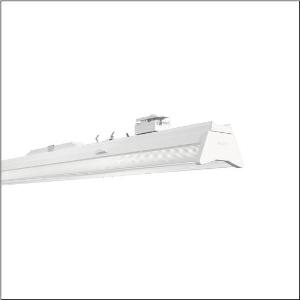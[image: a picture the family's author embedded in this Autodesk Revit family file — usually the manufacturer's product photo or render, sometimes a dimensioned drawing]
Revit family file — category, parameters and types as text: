
# Revit family: licross_21_performance_mo_52td16cn445g
name_source: partatom
category: Lighting Fixtures
units: mm (PartAtom-declared; Revit-internal decimal feet)

## family parameters
Cut with Voids When Loaded = No
Host = Face
Light Source = No
Part Type = Normal
Room Calculation Point = No
Round Connector Dimension = Use Diameter
Shared = No

## types (1)
- --- (1 x LED, 4500 lm, 24.1 W, 4000K)
    Apparent Load = 24 VA
    CIE Flux Codes = 66 88 96 79 100
    Color Rendering = 80
    Color Temperature = 4000K
    Default Elevation = 1800 mm
    Description = Licross 21 Performance MO, luminaire insert, of sheet steel, galvanised, coil coated, white, length: 1.500mm, width: 120mm, height: 123mm, LED rated luminous flux: 4.500lm, light colour: 840, SDCM (Standard Deviation of Colour Matching)MacAdam ≤ 3 SDCM (initial), control gear: ON/OFF Multilumen, CLOi, with plug, 3-pole, with phase selection, mains connection: 220..240V, AC, 50/60Hz, start of lifetime: 24W, end of service life: 28W, internal wiring halogen-free, primary light control with lens, of plastic, primary optical cover: cover, of PMMA, CAT 2 (L<= 3000cd/m²), light emission: direct/indirect distribution, primary light characteristic: symmetric, protection rating (complete): IP54, insulation class (complete): insulation class I (protective earthing), certification: CE, ENEC, UKCA, protection symbol: D if used in an environment with non-conductive dust loads with corresponding accessories, impact resistance: IK06, permissible ambient temperature for indoor applications: -35..+55°C, corresponds to IFS (International Featured Standards) requirements for safety and quality in the food industry, reducing of maximum allowable ambient temperature of 5°C with ceiling mounting, LABS conformity tested according to VDMA 24364:2018-05, The light source and the operating device comply with the requirements of the Ecodesign Regulation (EU) 2019/2020 and are replaceable in accordance with this regulation, packaging unit: 1 piece
    Height = 114 mm
    Lamp = 1 x LED
    Lamp Light Flux = 4500 lm
    Lamp Power = 24.1 W
    Lamp count = 1
    Length = 1500 mm
    Luminous efficacy = 187 lm/W
    Manufacturer = Siteco
    ModVariant = No
    Model = 52TD16CN445G
    Mounting Place = Ceiling
    Mounting Type = Pendant
    Number of Poles = 1
    OnlyDefault = Yes
    Power Factor = 1
    Product Name = Licross 21 Performance MO
    Product group = luminaire insert | ceiling pendant
    ProductGroupID = 901
    Protection Class = Protection class I
    Protection Degree = IP 54
    RLX_Detail_Level = 1
    RLX_Emergency_Light_Flux = 0 lm
    RLX_Emergency_Type = 0
    RLX_Emergency_Type_DB = No
    RlxData = <blob elided: 31709 chars, md5=b6a560fa>
    Socket = socket
    Standby Power = 0 W
    System Light Flux = 4500 lm
    System Power = 24 W
    Type Comments = factory setting: luminous flux: 100 % | (A | C | E) | 55 mA
    Type Image = l_1256138.jpg
    URL = http://relux.com
    VarID = @adj_057859
    Voltage = 0 V
    Weight = 0.00 kg
    Width = 120 mm

## geometry (parser evidence)
native form markers: Blend x4, Sweep x11
no freeform markers — native parametric forms only
